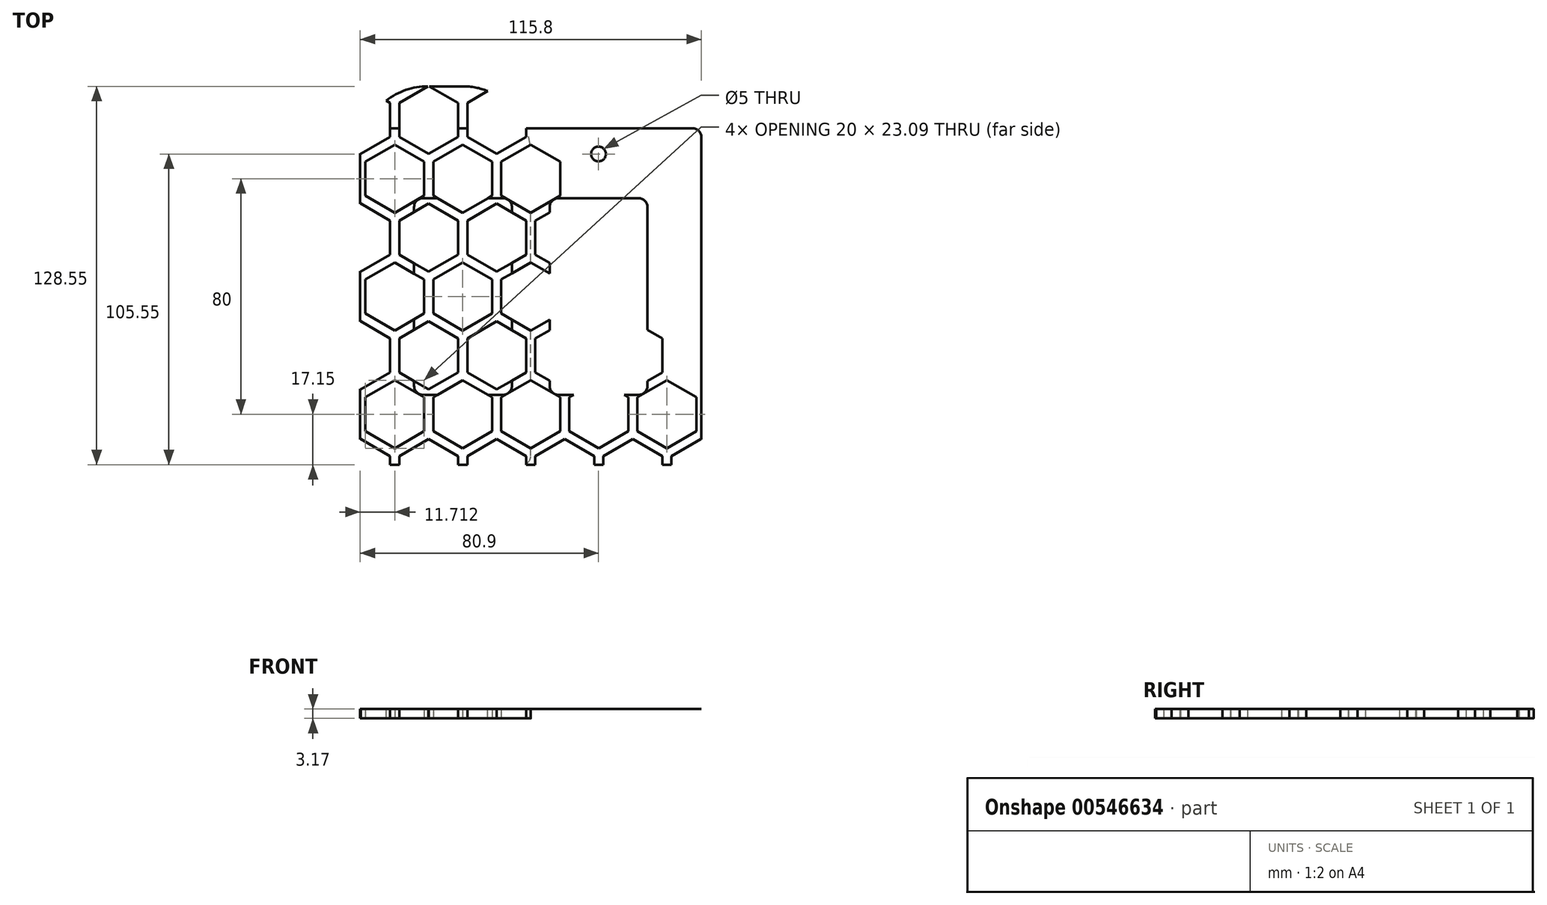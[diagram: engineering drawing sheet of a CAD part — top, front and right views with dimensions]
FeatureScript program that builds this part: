
annotation { "Feature Type Name" : "Feature", "Feature Type Description" : "" }
export const myFeature = defineFeature(function(context is Context, id is Id, definition is map)
    precondition{}
    {
        {
            var Q0;
            Q0=qCreatedBy(makeId("Top.planeOp"),FACE);
            var sketch = newSketch(context, id + "F0", { "sketchPlane" : qUnion([Q0])});
            skLineSegment(sketch, "E0", {"start": v(0, 57.15) * mm, "end": v(0, -57.15) * mm});
            skLineSegment(sketch, "E1.bottom", {"start": v(-6.4, -33.4) * mm, "end": v(-39.6, -33.4) * mm});
            skLineSegment(sketch, "E1.top", {"start": v(-6.4, 33.4) * mm, "end": v(-39.6, 33.4) * mm});
            skLineSegment(sketch, "E1.left", {"start": v(-6.4, -33.4) * mm, "end": v(-6.4, 33.4) * mm});
            skLineSegment(sketch, "E1.right", {"start": v(-39.6, -33.4) * mm, "end": v(-39.6, 33.4) * mm});
            skPoint(sketch, "E1.middle", {"position": v(-23, 0) * mm});
            skLineSegment(sketch, "E2.bottom", {"start": v(0, 57.15) * mm, "end": v(-57.9, 57.15) * mm});
            skLineSegment(sketch, "E2.top", {"start": v(0, -57.15) * mm, "end": v(-57.9, -57.15) * mm});
            skLineSegment(sketch, "E2.right", {"start": v(-57.9, 57.15) * mm, "end": v(-57.9, -57.15) * mm});
            skPoint(sketch, "E2.middle", {"position": v(-28.95, 0) * mm});
            skCircle(sketch, "E3", {"center": v(-23, 48.4) * mm, "radius": 2.5 * mm});
            skLineSegment(sketch, "E4", {"start": v(-23, 48.4) * mm, "end": v(-23, -48.4) * mm, "construction": true});
            skCircle(sketch, "E5", {"center": v(-23, -48.4) * mm, "radius": 2.5 * mm});
            skSolve(sketch);
        }
        {
            var Q0;
            Q0 = qSketchRegion(id + "F0", true);
            var Q1;
            Q1 = qConstructionFilter(qBodyType(qCreatedBy(id + "F0" ,EDGE), BodyType.WIRE), ConstructionObject.NO);
            extrude(context, id + "F1", {"entities" : qUnion([Q0]), "surfaceEntities" : qUnion([Q1]), "depth" : 1 / 203.2 * mm, "offsetDistance" : 25 * mm});
        }
        {
            var Q0;
            Q0=qCreatedBy(makeId("Top.planeOp"),FACE);
            var sketch = newSketch(context, id + "F2", { "sketchPlane" : qUnion([Q0])});
            skLineSegment(sketch, "E6.0.1", {"start": v(-57.9, 48.4) * mm, "end": v(-57.9, -57.15) * mm});
            skLineSegment(sketch, "E6.0.2", {"start": v(-57.9, -57.15) * mm, "end": v(0, -57.15) * mm});
            skLineSegment(sketch, "E6.0.3", {"start": v(0, -57.15) * mm, "end": v(0, 48.4) * mm});
            skCircle(sketch, "E7.0", {"center": v(-23, 48.4) * mm, "radius": 2.5 * mm});
            skLineSegment(sketch, "E7.1", {"start": v(-6.4, 33.4) * mm, "end": v(-39.6, 33.4) * mm, "construction": true});
            skLineSegment(sketch, "E7.2", {"start": v(-39.6, -33.4) * mm, "end": v(-39.6, 33.4) * mm, "construction": true});
            skLineSegment(sketch, "E7.3", {"start": v(-6.4, -33.4) * mm, "end": v(-6.4, 33.4) * mm, "construction": true});
            skLineSegment(sketch, "E7.4", {"start": v(-6.4, -33.4) * mm, "end": v(-39.6, -33.4) * mm, "construction": true});
            skCircle(sketch, "E8.0", {"center": v(-23, -48.4) * mm, "radius": 2.5 * mm});
            skLineSegment(sketch, "E9", {"start": v(0, 48.4) * mm, "end": v(0, 48.4) * mm});
            skArc(sketch, "E10", {"start": v(0, 48.4) * mm, "mid": v(-6.74, 64.66) * mm, "end": v(-23, 71.4) * mm});
            skArc(sketch, "E11", {"start": v(-57.9, 48.4) * mm, "mid": v(-51.16, 64.66) * mm, "end": v(-34.9, 71.4) * mm});
            skLineSegment(sketch, "E12", {"start": v(-34.9, 71.4) * mm, "end": v(-23, 71.4) * mm});
            skSolve(sketch);
        }
        {
            var Q0;
            Q0 = qSketchRegion(id + "F2", true);
            extrude(context, id + "F3", {"entities" : qUnion([Q0]), "oppositeDirection" : true, "depth" : 25.4 * mm / 8, "offsetDistance" : 25 * mm});
        }
        {
            var Q0;
            Q0=makeQuery(id+"F1.opExtrude","SWEPT_EDGE",EDGE,{"disambiguationData":[OSD([sQuery(id+"F0.wireOp",EDGE,"E2.bottom"),sQuery(id+"F0.wireOp",EDGE,"E2.right")])]});
            var Q1;
            Q1=makeQuery(id+"F1.opExtrude","SWEPT_EDGE",EDGE,{"disambiguationData":[OSD([sQuery(id+"F0.wireOp",EDGE,"E2.top"),sQuery(id+"F0.wireOp",EDGE,"E2.right")])]});
            var Q2;
            Q2=makeQuery(id+"F1.opExtrude","SWEPT_EDGE",EDGE,{"disambiguationData":[OSD([sQuery(id+"F0.wireOp",EDGE,"E1.top"),sQuery(id+"F0.wireOp",EDGE,"E1.right")])]});
            var Q3;
            Q3=makeQuery(id+"F1.opExtrude","SWEPT_EDGE",EDGE,{"disambiguationData":[OSD([sQuery(id+"F0.wireOp",EDGE,"E1.bottom"),sQuery(id+"F0.wireOp",EDGE,"E1.right")])]});
            var Q4;
            Q4=makeQuery(id+"F1.opExtrude","SWEPT_EDGE",EDGE,{"disambiguationData":[OSD([sQuery(id+"F0.wireOp",EDGE,"E1.bottom"),sQuery(id+"F0.wireOp",EDGE,"E1.left")])]});
            var Q5;
            Q5=makeQuery(id+"F1.opExtrude","SWEPT_EDGE",EDGE,{"disambiguationData":[OSD([sQuery(id+"F0.wireOp",EDGE,"E1.top"),sQuery(id+"F0.wireOp",EDGE,"E1.left")])]});
            var Q6;
            Q6=makeQuery(id+"F3.opExtrude","SWEPT_EDGE",EDGE,{"disambiguationData":[OSD([sQuery(id+"F2.wireOp",EDGE,"E6.0.0"),sQuery(id+"F2.wireOp",EDGE,"E6.0.3")])]});
            var Q7;
            Q7=makeQuery(id+"F3.opExtrude","SWEPT_EDGE",EDGE,{"disambiguationData":[OSD([sQuery(id+"F2.wireOp",EDGE,"E6.0.0"),sQuery(id+"F2.wireOp",EDGE,"E6.0.1")])]});
            var Q8;
            Q8=makeQuery(id+"F3.opExtrude","SWEPT_EDGE",EDGE,{"disambiguationData":[OSD([sQuery(id+"F2.wireOp",EDGE,"E6.0.2"),sQuery(id+"F2.wireOp",EDGE,"E6.0.3")])]});
            var Q9;
            Q9=makeQuery(id+"F3.opExtrude","SWEPT_EDGE",EDGE,{"disambiguationData":[OSD([sQuery(id+"F2.wireOp",EDGE,"E6.0.1"),sQuery(id+"F2.wireOp",EDGE,"E6.0.2")])]});
            fillet(context, id + "F4", {"entities" : qUnion([Q0, Q1, Q2, Q3, Q4, Q5, Q6, Q7, Q8, Q9]), "radius" : 3 * mm, "tangentPropagation" : true, "allowEdgeOverflow" : false});
        }
        {
            var Q0;
            Q0=makeQuery(id+"F1.opExtrude","SWEPT_BODY",BODY,{"disambiguationData":[OSD([sQuery(id+"F0.wireOp",EDGE,"E0"),sQuery(id+"F0.wireOp",EDGE,"E1.bottom"),sQuery(id+"F0.wireOp",EDGE,"E1.top"),sQuery(id+"F0.wireOp",EDGE,"E1.left"),sQuery(id+"F0.wireOp",EDGE,"E1.right"),sQuery(id+"F0.wireOp",EDGE,"E2.bottom"),sQuery(id+"F0.wireOp",EDGE,"E2.top"),sQuery(id+"F0.wireOp",EDGE,"E2.right"),sQuery(id+"F0.wireOp",EDGE,"E3"),sQuery(id+"F0.wireOp",EDGE,"E5")])]});
            var Q1;
            Q1=makeQuery(id+"F1.opExtrude","SWEPT_FACE",FACE,{"disambiguationData":[OSD([sQuery(id+"F0.wireOp",EDGE,"E0")])]});
            mirror(context, id + "F5", {"operationType" : NewBodyOperationType.ADD, "entities" : qUnion([Q0]), "mirrorPlane" : qUnion([Q1])});
        }
        {
            var Q0;
            Q0=makeQuery(id+"F3.opExtrude","CAP_FACE",FACE,{"disambiguationData":[OSD([sQuery(id+"F2.wireOp",EDGE,"E6.0.1"),sQuery(id+"F2.wireOp",EDGE,"E6.0.2"),sQuery(id+"F2.wireOp",EDGE,"E6.0.3"),sQuery(id+"F2.wireOp",EDGE,"E7.0"),sQuery(id+"F2.wireOp",EDGE,"E8.0"),sQuery(id+"F2.wireOp",EDGE,"E10"),sQuery(id+"F2.wireOp",EDGE,"E11"),sQuery(id+"F2.wireOp",EDGE,"E12")])],"isStart":false});
            var sketch = newSketch(context, id + "F6", { "sketchPlane" : qUnion([Q0])});
            skCircle(sketch, "E13.cCircle", {"center": v(57.74, 60) * mm, "radius": 11.55 * mm, "construction": true});
            skLineSegment(sketch, "E13.0", {"start": v(47.74, 65.77) * mm, "end": v(57.74, 71.55) * mm});
            skLineSegment(sketch, "E13.1", {"start": v(57.74, 71.55) * mm, "end": v(67.74, 65.77) * mm});
            skLineSegment(sketch, "E13.2", {"start": v(67.74, 65.77) * mm, "end": v(67.74, 54.23) * mm});
            skLineSegment(sketch, "E13.3", {"start": v(67.74, 54.23) * mm, "end": v(57.74, 48.45) * mm});
            skLineSegment(sketch, "E13.4", {"start": v(57.74, 48.45) * mm, "end": v(47.74, 54.23) * mm});
            skLineSegment(sketch, "E13.5", {"start": v(47.74, 54.23) * mm, "end": v(47.74, 65.77) * mm});
            skLineSegment(sketch, "E14.0.1.0", {"start": v(36.19, 34.23) * mm, "end": v(36.19, 45.77) * mm});
            skLineSegment(sketch, "E14.0.1.1", {"start": v(46.19, 28.45) * mm, "end": v(36.19, 34.23) * mm});
            skLineSegment(sketch, "E14.0.1.2", {"start": v(56.19, 34.23) * mm, "end": v(46.19, 28.45) * mm});
            skLineSegment(sketch, "E14.0.1.3", {"start": v(56.19, 45.77) * mm, "end": v(56.19, 34.23) * mm});
            skLineSegment(sketch, "E14.0.1.4", {"start": v(46.19, 51.55) * mm, "end": v(56.19, 45.77) * mm});
            skCircle(sketch, "E14.0.1.5", {"center": v(46.19, 40) * mm, "radius": 11.55 * mm, "construction": true});
            skLineSegment(sketch, "E14.0.1.6", {"start": v(36.19, 45.77) * mm, "end": v(46.19, 51.55) * mm});
            skLineSegment(sketch, "E14.0.2.0", {"start": v(24.64, 14.23) * mm, "end": v(24.64, 25.77) * mm});
            skLineSegment(sketch, "E14.0.2.1", {"start": v(34.64, 8.45) * mm, "end": v(24.64, 14.23) * mm});
            skLineSegment(sketch, "E14.0.2.2", {"start": v(44.64, 14.23) * mm, "end": v(34.64, 8.45) * mm});
            skLineSegment(sketch, "E14.0.2.3", {"start": v(44.64, 25.77) * mm, "end": v(44.64, 14.23) * mm});
            skLineSegment(sketch, "E14.0.2.4", {"start": v(34.64, 31.55) * mm, "end": v(44.64, 25.77) * mm});
            skCircle(sketch, "E14.0.2.5", {"center": v(34.64, 20) * mm, "radius": 11.55 * mm, "construction": true});
            skLineSegment(sketch, "E14.0.2.6", {"start": v(24.64, 25.77) * mm, "end": v(34.64, 31.55) * mm});
            skLineSegment(sketch, "E14.0.3.0", {"start": v(13.1, -5.77) * mm, "end": v(13.1, 5.77) * mm});
            skLineSegment(sketch, "E14.0.3.1", {"start": v(23.1, -11.55) * mm, "end": v(13.1, -5.77) * mm});
            skLineSegment(sketch, "E14.0.3.2", {"start": v(33.1, -5.77) * mm, "end": v(23.1, -11.55) * mm});
            skLineSegment(sketch, "E14.0.3.3", {"start": v(33.1, 5.77) * mm, "end": v(33.1, -5.77) * mm});
            skLineSegment(sketch, "E14.0.3.4", {"start": v(23.1, 11.55) * mm, "end": v(33.1, 5.77) * mm});
            skCircle(sketch, "E14.0.3.5", {"center": v(23.1, 0) * mm, "radius": 11.55 * mm, "construction": true});
            skLineSegment(sketch, "E14.0.3.6", {"start": v(13.1, 5.77) * mm, "end": v(23.1, 11.55) * mm});
            skLineSegment(sketch, "E14.0.4.0", {"start": v(1.55, -25.77) * mm, "end": v(1.55, -14.23) * mm});
            skLineSegment(sketch, "E14.0.4.1", {"start": v(11.55, -31.55) * mm, "end": v(1.55, -25.77) * mm});
            skLineSegment(sketch, "E14.0.4.2", {"start": v(21.55, -25.77) * mm, "end": v(11.55, -31.55) * mm});
            skLineSegment(sketch, "E14.0.4.3", {"start": v(21.55, -14.23) * mm, "end": v(21.55, -25.77) * mm});
            skLineSegment(sketch, "E14.0.4.4", {"start": v(11.55, -8.45) * mm, "end": v(21.55, -14.23) * mm});
            skCircle(sketch, "E14.0.4.5", {"center": v(11.55, -20) * mm, "radius": 11.55 * mm, "construction": true});
            skLineSegment(sketch, "E14.0.4.6", {"start": v(1.55, -14.23) * mm, "end": v(11.55, -8.45) * mm});
            skLineSegment(sketch, "E14.1.0.0", {"start": v(24.64, 54.23) * mm, "end": v(24.64, 65.77) * mm});
            skLineSegment(sketch, "E14.1.0.1", {"start": v(34.64, 48.45) * mm, "end": v(24.64, 54.23) * mm});
            skLineSegment(sketch, "E14.1.0.2", {"start": v(44.64, 54.23) * mm, "end": v(34.64, 48.45) * mm});
            skLineSegment(sketch, "E14.1.0.3", {"start": v(44.64, 65.77) * mm, "end": v(44.64, 54.23) * mm});
            skLineSegment(sketch, "E14.1.0.4", {"start": v(34.64, 71.55) * mm, "end": v(44.64, 65.77) * mm});
            skCircle(sketch, "E14.1.0.5", {"center": v(34.64, 60) * mm, "radius": 11.55 * mm, "construction": true});
            skLineSegment(sketch, "E14.1.0.6", {"start": v(24.64, 65.77) * mm, "end": v(34.64, 71.55) * mm});
            skLineSegment(sketch, "E14.1.1.0", {"start": v(13.1, 34.23) * mm, "end": v(13.1, 45.77) * mm});
            skLineSegment(sketch, "E14.1.1.1", {"start": v(23.1, 28.45) * mm, "end": v(13.1, 34.23) * mm});
            skLineSegment(sketch, "E14.1.1.2", {"start": v(33.1, 34.23) * mm, "end": v(23.1, 28.45) * mm});
            skLineSegment(sketch, "E14.1.1.3", {"start": v(33.1, 45.77) * mm, "end": v(33.1, 34.23) * mm});
            skLineSegment(sketch, "E14.1.1.4", {"start": v(23.1, 51.55) * mm, "end": v(33.1, 45.77) * mm});
            skCircle(sketch, "E14.1.1.5", {"center": v(23.1, 40) * mm, "radius": 11.55 * mm, "construction": true});
            skLineSegment(sketch, "E14.1.1.6", {"start": v(13.1, 45.77) * mm, "end": v(23.1, 51.55) * mm});
            skLineSegment(sketch, "E14.1.2.0", {"start": v(1.55, 14.23) * mm, "end": v(1.55, 25.77) * mm});
            skLineSegment(sketch, "E14.1.2.1", {"start": v(11.55, 8.45) * mm, "end": v(1.55, 14.23) * mm});
            skLineSegment(sketch, "E14.1.2.2", {"start": v(21.55, 14.23) * mm, "end": v(11.55, 8.45) * mm});
            skLineSegment(sketch, "E14.1.2.3", {"start": v(21.55, 25.77) * mm, "end": v(21.55, 14.23) * mm});
            skLineSegment(sketch, "E14.1.2.4", {"start": v(11.55, 31.55) * mm, "end": v(21.55, 25.77) * mm});
            skCircle(sketch, "E14.1.2.5", {"center": v(11.55, 20) * mm, "radius": 11.55 * mm, "construction": true});
            skLineSegment(sketch, "E14.1.2.6", {"start": v(1.55, 25.77) * mm, "end": v(11.55, 31.55) * mm});
            skLineSegment(sketch, "E14.1.3.0", {"start": v(-10, -5.77) * mm, "end": v(-10, 5.77) * mm});
            skLineSegment(sketch, "E14.1.3.1", {"start": v(0, -11.55) * mm, "end": v(-10, -5.77) * mm});
            skLineSegment(sketch, "E14.1.3.2", {"start": v(10, -5.77) * mm, "end": v(0, -11.55) * mm});
            skLineSegment(sketch, "E14.1.3.3", {"start": v(10, 5.77) * mm, "end": v(10, -5.77) * mm});
            skLineSegment(sketch, "E14.1.3.4", {"start": v(0, 11.55) * mm, "end": v(10, 5.77) * mm});
            skCircle(sketch, "E14.1.3.5", {"center": v(0, 0) * mm, "radius": 11.55 * mm, "construction": true});
            skLineSegment(sketch, "E14.1.3.6", {"start": v(-10, 5.77) * mm, "end": v(0, 11.55) * mm});
            skLineSegment(sketch, "E14.1.4.0", {"start": v(-21.55, -25.77) * mm, "end": v(-21.55, -14.23) * mm});
            skLineSegment(sketch, "E14.1.4.1", {"start": v(-11.55, -31.55) * mm, "end": v(-21.55, -25.77) * mm});
            skLineSegment(sketch, "E14.1.4.2", {"start": v(-1.55, -25.77) * mm, "end": v(-11.55, -31.55) * mm});
            skLineSegment(sketch, "E14.1.4.3", {"start": v(-1.55, -14.23) * mm, "end": v(-1.55, -25.77) * mm});
            skLineSegment(sketch, "E14.1.4.4", {"start": v(-11.55, -8.45) * mm, "end": v(-1.55, -14.23) * mm});
            skCircle(sketch, "E14.1.4.5", {"center": v(-11.55, -20) * mm, "radius": 11.55 * mm, "construction": true});
            skLineSegment(sketch, "E14.1.4.6", {"start": v(-21.55, -14.23) * mm, "end": v(-11.55, -8.45) * mm});
            skLineSegment(sketch, "E14.2.0.0", {"start": v(1.55, 54.23) * mm, "end": v(1.55, 65.77) * mm});
            skLineSegment(sketch, "E14.2.0.1", {"start": v(11.55, 48.45) * mm, "end": v(1.55, 54.23) * mm});
            skLineSegment(sketch, "E14.2.0.2", {"start": v(21.55, 54.23) * mm, "end": v(11.55, 48.45) * mm});
            skLineSegment(sketch, "E14.2.0.3", {"start": v(21.55, 65.77) * mm, "end": v(21.55, 54.23) * mm});
            skLineSegment(sketch, "E14.2.0.4", {"start": v(11.55, 71.55) * mm, "end": v(21.55, 65.77) * mm});
            skCircle(sketch, "E14.2.0.5", {"center": v(11.55, 60) * mm, "radius": 11.55 * mm, "construction": true});
            skLineSegment(sketch, "E14.2.0.6", {"start": v(1.55, 65.77) * mm, "end": v(11.55, 71.55) * mm});
            skLineSegment(sketch, "E14.2.1.0", {"start": v(-10, 34.23) * mm, "end": v(-10, 45.77) * mm});
            skLineSegment(sketch, "E14.2.1.1", {"start": v(0, 28.45) * mm, "end": v(-10, 34.23) * mm});
            skLineSegment(sketch, "E14.2.1.2", {"start": v(10, 34.23) * mm, "end": v(0, 28.45) * mm});
            skLineSegment(sketch, "E14.2.1.3", {"start": v(10, 45.77) * mm, "end": v(10, 34.23) * mm});
            skLineSegment(sketch, "E14.2.1.4", {"start": v(0, 51.55) * mm, "end": v(10, 45.77) * mm});
            skCircle(sketch, "E14.2.1.5", {"center": v(0, 40) * mm, "radius": 11.55 * mm, "construction": true});
            skLineSegment(sketch, "E14.2.1.6", {"start": v(-10, 45.77) * mm, "end": v(0, 51.55) * mm});
            skLineSegment(sketch, "E14.2.2.0", {"start": v(-21.55, 14.23) * mm, "end": v(-21.55, 25.77) * mm});
            skLineSegment(sketch, "E14.2.2.1", {"start": v(-11.55, 8.45) * mm, "end": v(-21.55, 14.23) * mm});
            skLineSegment(sketch, "E14.2.2.2", {"start": v(-1.55, 14.23) * mm, "end": v(-11.55, 8.45) * mm});
            skLineSegment(sketch, "E14.2.2.3", {"start": v(-1.55, 25.77) * mm, "end": v(-1.55, 14.23) * mm});
            skLineSegment(sketch, "E14.2.2.4", {"start": v(-11.55, 31.55) * mm, "end": v(-1.55, 25.77) * mm});
            skCircle(sketch, "E14.2.2.5", {"center": v(-11.55, 20) * mm, "radius": 11.55 * mm, "construction": true});
            skLineSegment(sketch, "E14.2.2.6", {"start": v(-21.55, 25.77) * mm, "end": v(-11.55, 31.55) * mm});
            skLineSegment(sketch, "E14.2.3.0", {"start": v(-33.1, -5.77) * mm, "end": v(-33.1, 5.77) * mm});
            skLineSegment(sketch, "E14.2.3.1", {"start": v(-23.1, -11.55) * mm, "end": v(-33.1, -5.77) * mm});
            skLineSegment(sketch, "E14.2.3.2", {"start": v(-13.1, -5.77) * mm, "end": v(-23.1, -11.55) * mm});
            skLineSegment(sketch, "E14.2.3.3", {"start": v(-13.1, 5.77) * mm, "end": v(-13.1, -5.77) * mm});
            skLineSegment(sketch, "E14.2.3.4", {"start": v(-23.1, 11.55) * mm, "end": v(-13.1, 5.77) * mm});
            skCircle(sketch, "E14.2.3.5", {"center": v(-23.1, 0) * mm, "radius": 11.55 * mm, "construction": true});
            skLineSegment(sketch, "E14.2.3.6", {"start": v(-33.1, 5.77) * mm, "end": v(-23.1, 11.55) * mm});
            skLineSegment(sketch, "E14.2.4.0", {"start": v(-44.64, -25.77) * mm, "end": v(-44.64, -14.23) * mm});
            skLineSegment(sketch, "E14.2.4.1", {"start": v(-34.64, -31.55) * mm, "end": v(-44.64, -25.77) * mm});
            skLineSegment(sketch, "E14.2.4.2", {"start": v(-24.64, -25.77) * mm, "end": v(-34.64, -31.55) * mm});
            skLineSegment(sketch, "E14.2.4.3", {"start": v(-24.64, -14.23) * mm, "end": v(-24.64, -25.77) * mm});
            skLineSegment(sketch, "E14.2.4.4", {"start": v(-34.64, -8.45) * mm, "end": v(-24.64, -14.23) * mm});
            skCircle(sketch, "E14.2.4.5", {"center": v(-34.64, -20) * mm, "radius": 11.55 * mm, "construction": true});
            skLineSegment(sketch, "E14.2.4.6", {"start": v(-44.64, -14.23) * mm, "end": v(-34.64, -8.45) * mm});
            skLineSegment(sketch, "E14.direction1", {"start": v(47.74, 54.23) * mm, "end": v(24.64, 54.23) * mm, "construction": true});
            skLineSegment(sketch, "E14.direction2", {"start": v(47.74, 54.23) * mm, "end": v(36.19, 34.23) * mm, "construction": true});
            skLineSegment(sketch, "E15.0.0.5", {"start": v(-10, -45.77) * mm, "end": v(-10, -34.23) * mm});
            skLineSegment(sketch, "E15.3.0.5", {"start": v(0, -51.55) * mm, "end": v(-10, -45.77) * mm});
            skLineSegment(sketch, "E15.6.0.5", {"start": v(10, -45.77) * mm, "end": v(0, -51.55) * mm});
            skLineSegment(sketch, "E15.9.0.5", {"start": v(10, -34.23) * mm, "end": v(10, -45.77) * mm});
            skLineSegment(sketch, "E15.12.0.5", {"start": v(0, -28.45) * mm, "end": v(10, -34.23) * mm});
            skCircle(sketch, "E15.15.0.5", {"center": v(0, -40) * mm, "radius": 11.55 * mm, "construction": true});
            skLineSegment(sketch, "E15.17.0.5", {"start": v(-10, -34.23) * mm, "end": v(0, -28.45) * mm});
            skLineSegment(sketch, "E15.0.0.6", {"start": v(-21.55, -65.77) * mm, "end": v(-21.55, -54.23) * mm});
            skLineSegment(sketch, "E15.3.0.6", {"start": v(-11.55, -71.55) * mm, "end": v(-21.55, -65.77) * mm});
            skLineSegment(sketch, "E15.6.0.6", {"start": v(-1.55, -65.77) * mm, "end": v(-11.55, -71.55) * mm});
            skLineSegment(sketch, "E15.9.0.6", {"start": v(-1.55, -54.23) * mm, "end": v(-1.55, -65.77) * mm});
            skLineSegment(sketch, "E15.12.0.6", {"start": v(-11.55, -48.45) * mm, "end": v(-1.55, -54.23) * mm});
            skCircle(sketch, "E15.15.0.6", {"center": v(-11.55, -60) * mm, "radius": 11.55 * mm, "construction": true});
            skLineSegment(sketch, "E15.17.0.6", {"start": v(-21.55, -54.23) * mm, "end": v(-11.55, -48.45) * mm});
            skLineSegment(sketch, "E15.0.1.5", {"start": v(-33.1, -45.77) * mm, "end": v(-33.1, -34.23) * mm});
            skLineSegment(sketch, "E15.3.1.5", {"start": v(-23.1, -51.55) * mm, "end": v(-33.1, -45.77) * mm});
            skLineSegment(sketch, "E15.6.1.5", {"start": v(-13.1, -45.77) * mm, "end": v(-23.1, -51.55) * mm});
            skLineSegment(sketch, "E15.9.1.5", {"start": v(-13.1, -34.23) * mm, "end": v(-13.1, -45.77) * mm});
            skLineSegment(sketch, "E15.12.1.5", {"start": v(-23.1, -28.45) * mm, "end": v(-13.1, -34.23) * mm});
            skCircle(sketch, "E15.15.1.5", {"center": v(-23.1, -40) * mm, "radius": 11.55 * mm, "construction": true});
            skLineSegment(sketch, "E15.17.1.5", {"start": v(-33.1, -34.23) * mm, "end": v(-23.1, -28.45) * mm});
            skLineSegment(sketch, "E15.0.1.6", {"start": v(-44.64, -65.77) * mm, "end": v(-44.64, -54.23) * mm});
            skLineSegment(sketch, "E15.3.1.6", {"start": v(-34.64, -71.55) * mm, "end": v(-44.64, -65.77) * mm});
            skLineSegment(sketch, "E15.6.1.6", {"start": v(-24.64, -65.77) * mm, "end": v(-34.64, -71.55) * mm});
            skLineSegment(sketch, "E15.9.1.6", {"start": v(-24.64, -54.23) * mm, "end": v(-24.64, -65.77) * mm});
            skLineSegment(sketch, "E15.12.1.6", {"start": v(-34.64, -48.45) * mm, "end": v(-24.64, -54.23) * mm});
            skCircle(sketch, "E15.15.1.6", {"center": v(-34.64, -60) * mm, "radius": 11.55 * mm, "construction": true});
            skLineSegment(sketch, "E15.17.1.6", {"start": v(-44.64, -54.23) * mm, "end": v(-34.64, -48.45) * mm});
            skLineSegment(sketch, "E15.0.2.5", {"start": v(-56.19, -45.77) * mm, "end": v(-56.19, -34.23) * mm});
            skLineSegment(sketch, "E15.3.2.5", {"start": v(-46.19, -51.55) * mm, "end": v(-56.19, -45.77) * mm});
            skLineSegment(sketch, "E15.6.2.5", {"start": v(-36.19, -45.77) * mm, "end": v(-46.19, -51.55) * mm});
            skLineSegment(sketch, "E15.9.2.5", {"start": v(-36.19, -34.23) * mm, "end": v(-36.19, -45.77) * mm});
            skLineSegment(sketch, "E15.12.2.5", {"start": v(-46.19, -28.45) * mm, "end": v(-36.19, -34.23) * mm});
            skCircle(sketch, "E15.15.2.5", {"center": v(-46.19, -40) * mm, "radius": 11.55 * mm, "construction": true});
            skLineSegment(sketch, "E15.17.2.5", {"start": v(-56.19, -34.23) * mm, "end": v(-46.19, -28.45) * mm});
            skLineSegment(sketch, "E15.0.2.6", {"start": v(-67.74, -65.77) * mm, "end": v(-67.74, -54.23) * mm});
            skLineSegment(sketch, "E15.3.2.6", {"start": v(-57.74, -71.55) * mm, "end": v(-67.74, -65.77) * mm});
            skLineSegment(sketch, "E15.6.2.6", {"start": v(-47.74, -65.77) * mm, "end": v(-57.74, -71.55) * mm});
            skLineSegment(sketch, "E15.9.2.6", {"start": v(-47.74, -54.23) * mm, "end": v(-47.74, -65.77) * mm});
            skLineSegment(sketch, "E15.12.2.6", {"start": v(-57.74, -48.45) * mm, "end": v(-47.74, -54.23) * mm});
            skCircle(sketch, "E15.15.2.6", {"center": v(-57.74, -60) * mm, "radius": 11.55 * mm, "construction": true});
            skLineSegment(sketch, "E15.17.2.6", {"start": v(-67.74, -54.23) * mm, "end": v(-57.74, -48.45) * mm});
            skLineSegment(sketch, "E16.0.3.0", {"start": v(-21.55, 54.23) * mm, "end": v(-21.55, 65.77) * mm});
            skLineSegment(sketch, "E16.3.3.0", {"start": v(-11.55, 48.45) * mm, "end": v(-21.55, 54.23) * mm});
            skLineSegment(sketch, "E16.6.3.0", {"start": v(-1.55, 54.23) * mm, "end": v(-11.55, 48.45) * mm});
            skLineSegment(sketch, "E16.9.3.0", {"start": v(-1.55, 65.77) * mm, "end": v(-1.55, 54.23) * mm});
            skLineSegment(sketch, "E16.12.3.0", {"start": v(-11.55, 71.55) * mm, "end": v(-1.55, 65.77) * mm});
            skCircle(sketch, "E16.15.3.0", {"center": v(-11.55, 60) * mm, "radius": 11.55 * mm, "construction": true});
            skLineSegment(sketch, "E16.17.3.0", {"start": v(-21.55, 65.77) * mm, "end": v(-11.55, 71.55) * mm});
            skLineSegment(sketch, "E16.0.3.1", {"start": v(-33.1, 34.23) * mm, "end": v(-33.1, 45.77) * mm});
            skLineSegment(sketch, "E16.3.3.1", {"start": v(-23.1, 28.45) * mm, "end": v(-33.1, 34.23) * mm});
            skLineSegment(sketch, "E16.6.3.1", {"start": v(-13.1, 34.23) * mm, "end": v(-23.1, 28.45) * mm});
            skLineSegment(sketch, "E16.9.3.1", {"start": v(-13.1, 45.77) * mm, "end": v(-13.1, 34.23) * mm});
            skLineSegment(sketch, "E16.12.3.1", {"start": v(-23.1, 51.55) * mm, "end": v(-13.1, 45.77) * mm});
            skCircle(sketch, "E16.15.3.1", {"center": v(-23.1, 40) * mm, "radius": 11.55 * mm, "construction": true});
            skLineSegment(sketch, "E16.17.3.1", {"start": v(-33.1, 45.77) * mm, "end": v(-23.1, 51.55) * mm});
            skLineSegment(sketch, "E16.0.3.2", {"start": v(-44.64, 14.23) * mm, "end": v(-44.64, 25.77) * mm});
            skLineSegment(sketch, "E16.3.3.2", {"start": v(-34.64, 8.45) * mm, "end": v(-44.64, 14.23) * mm});
            skLineSegment(sketch, "E16.6.3.2", {"start": v(-24.64, 14.23) * mm, "end": v(-34.64, 8.45) * mm});
            skLineSegment(sketch, "E16.9.3.2", {"start": v(-24.64, 25.77) * mm, "end": v(-24.64, 14.23) * mm});
            skLineSegment(sketch, "E16.12.3.2", {"start": v(-34.64, 31.55) * mm, "end": v(-24.64, 25.77) * mm});
            skCircle(sketch, "E16.15.3.2", {"center": v(-34.64, 20) * mm, "radius": 11.55 * mm, "construction": true});
            skLineSegment(sketch, "E16.17.3.2", {"start": v(-44.64, 25.77) * mm, "end": v(-34.64, 31.55) * mm});
            skLineSegment(sketch, "E16.0.3.3", {"start": v(-56.19, -5.77) * mm, "end": v(-56.19, 5.77) * mm});
            skLineSegment(sketch, "E16.3.3.3", {"start": v(-46.19, -11.55) * mm, "end": v(-56.19, -5.77) * mm});
            skLineSegment(sketch, "E16.6.3.3", {"start": v(-36.19, -5.77) * mm, "end": v(-46.19, -11.55) * mm});
            skLineSegment(sketch, "E16.9.3.3", {"start": v(-36.19, 5.77) * mm, "end": v(-36.19, -5.77) * mm});
            skLineSegment(sketch, "E16.12.3.3", {"start": v(-46.19, 11.55) * mm, "end": v(-36.19, 5.77) * mm});
            skCircle(sketch, "E16.15.3.3", {"center": v(-46.19, 0) * mm, "radius": 11.55 * mm, "construction": true});
            skLineSegment(sketch, "E16.17.3.3", {"start": v(-56.19, 5.77) * mm, "end": v(-46.19, 11.55) * mm});
            skLineSegment(sketch, "E16.0.3.4", {"start": v(-67.74, -25.77) * mm, "end": v(-67.74, -14.23) * mm});
            skLineSegment(sketch, "E16.3.3.4", {"start": v(-57.74, -31.55) * mm, "end": v(-67.74, -25.77) * mm});
            skLineSegment(sketch, "E16.6.3.4", {"start": v(-47.74, -25.77) * mm, "end": v(-57.74, -31.55) * mm});
            skLineSegment(sketch, "E16.9.3.4", {"start": v(-47.74, -14.23) * mm, "end": v(-47.74, -25.77) * mm});
            skLineSegment(sketch, "E16.12.3.4", {"start": v(-57.74, -8.45) * mm, "end": v(-47.74, -14.23) * mm});
            skCircle(sketch, "E16.15.3.4", {"center": v(-57.74, -20) * mm, "radius": 11.55 * mm, "construction": true});
            skLineSegment(sketch, "E16.17.3.4", {"start": v(-67.74, -14.23) * mm, "end": v(-57.74, -8.45) * mm});
            skLineSegment(sketch, "E16.0.3.5", {"start": v(-79.28, -45.77) * mm, "end": v(-79.28, -34.23) * mm});
            skLineSegment(sketch, "E16.3.3.5", {"start": v(-69.28, -51.55) * mm, "end": v(-79.28, -45.77) * mm});
            skLineSegment(sketch, "E16.6.3.5", {"start": v(-59.28, -45.77) * mm, "end": v(-69.28, -51.55) * mm});
            skLineSegment(sketch, "E16.9.3.5", {"start": v(-59.28, -34.23) * mm, "end": v(-59.28, -45.77) * mm});
            skLineSegment(sketch, "E16.12.3.5", {"start": v(-69.28, -28.45) * mm, "end": v(-59.28, -34.23) * mm});
            skCircle(sketch, "E16.15.3.5", {"center": v(-69.28, -40) * mm, "radius": 11.55 * mm, "construction": true});
            skLineSegment(sketch, "E16.17.3.5", {"start": v(-79.28, -34.23) * mm, "end": v(-69.28, -28.45) * mm});
            skLineSegment(sketch, "E16.0.3.6", {"start": v(-90.83, -65.77) * mm, "end": v(-90.83, -54.23) * mm});
            skLineSegment(sketch, "E16.3.3.6", {"start": v(-80.83, -71.55) * mm, "end": v(-90.83, -65.77) * mm});
            skLineSegment(sketch, "E16.6.3.6", {"start": v(-70.83, -65.77) * mm, "end": v(-80.83, -71.55) * mm});
            skLineSegment(sketch, "E16.9.3.6", {"start": v(-70.83, -54.23) * mm, "end": v(-70.83, -65.77) * mm});
            skLineSegment(sketch, "E16.12.3.6", {"start": v(-80.83, -48.45) * mm, "end": v(-70.83, -54.23) * mm});
            skCircle(sketch, "E16.15.3.6", {"center": v(-80.83, -60) * mm, "radius": 11.55 * mm, "construction": true});
            skLineSegment(sketch, "E16.17.3.6", {"start": v(-90.83, -54.23) * mm, "end": v(-80.83, -48.45) * mm});
            skLineSegment(sketch, "E16.0.4.0", {"start": v(-44.64, 54.23) * mm, "end": v(-44.64, 65.77) * mm});
            skLineSegment(sketch, "E16.3.4.0", {"start": v(-34.64, 48.45) * mm, "end": v(-44.64, 54.23) * mm});
            skLineSegment(sketch, "E16.6.4.0", {"start": v(-24.64, 54.23) * mm, "end": v(-34.64, 48.45) * mm});
            skLineSegment(sketch, "E16.9.4.0", {"start": v(-24.64, 65.77) * mm, "end": v(-24.64, 54.23) * mm});
            skLineSegment(sketch, "E16.12.4.0", {"start": v(-34.64, 71.55) * mm, "end": v(-24.64, 65.77) * mm});
            skCircle(sketch, "E16.15.4.0", {"center": v(-34.64, 60) * mm, "radius": 11.55 * mm, "construction": true});
            skLineSegment(sketch, "E16.17.4.0", {"start": v(-44.64, 65.77) * mm, "end": v(-34.64, 71.55) * mm});
            skLineSegment(sketch, "E16.0.4.1", {"start": v(-56.19, 34.23) * mm, "end": v(-56.19, 45.77) * mm});
            skLineSegment(sketch, "E16.3.4.1", {"start": v(-46.19, 28.45) * mm, "end": v(-56.19, 34.23) * mm});
            skLineSegment(sketch, "E16.6.4.1", {"start": v(-36.19, 34.23) * mm, "end": v(-46.19, 28.45) * mm});
            skLineSegment(sketch, "E16.9.4.1", {"start": v(-36.19, 45.77) * mm, "end": v(-36.19, 34.23) * mm});
            skLineSegment(sketch, "E16.12.4.1", {"start": v(-46.19, 51.55) * mm, "end": v(-36.19, 45.77) * mm});
            skCircle(sketch, "E16.15.4.1", {"center": v(-46.19, 40) * mm, "radius": 11.55 * mm, "construction": true});
            skLineSegment(sketch, "E16.17.4.1", {"start": v(-56.19, 45.77) * mm, "end": v(-46.19, 51.55) * mm});
            skLineSegment(sketch, "E16.0.4.2", {"start": v(-67.74, 14.23) * mm, "end": v(-67.74, 25.77) * mm});
            skLineSegment(sketch, "E16.3.4.2", {"start": v(-57.74, 8.45) * mm, "end": v(-67.74, 14.23) * mm});
            skLineSegment(sketch, "E16.6.4.2", {"start": v(-47.74, 14.23) * mm, "end": v(-57.74, 8.45) * mm});
            skLineSegment(sketch, "E16.9.4.2", {"start": v(-47.74, 25.77) * mm, "end": v(-47.74, 14.23) * mm});
            skLineSegment(sketch, "E16.12.4.2", {"start": v(-57.74, 31.55) * mm, "end": v(-47.74, 25.77) * mm});
            skCircle(sketch, "E16.15.4.2", {"center": v(-57.74, 20) * mm, "radius": 11.55 * mm, "construction": true});
            skLineSegment(sketch, "E16.17.4.2", {"start": v(-67.74, 25.77) * mm, "end": v(-57.74, 31.55) * mm});
            skLineSegment(sketch, "E16.0.4.3", {"start": v(-79.28, -5.77) * mm, "end": v(-79.28, 5.77) * mm});
            skLineSegment(sketch, "E16.3.4.3", {"start": v(-69.28, -11.55) * mm, "end": v(-79.28, -5.77) * mm});
            skLineSegment(sketch, "E16.6.4.3", {"start": v(-59.28, -5.77) * mm, "end": v(-69.28, -11.55) * mm});
            skLineSegment(sketch, "E16.9.4.3", {"start": v(-59.28, 5.77) * mm, "end": v(-59.28, -5.77) * mm});
            skLineSegment(sketch, "E16.12.4.3", {"start": v(-69.28, 11.55) * mm, "end": v(-59.28, 5.77) * mm});
            skCircle(sketch, "E16.15.4.3", {"center": v(-69.28, 0) * mm, "radius": 11.55 * mm, "construction": true});
            skLineSegment(sketch, "E16.17.4.3", {"start": v(-79.28, 5.77) * mm, "end": v(-69.28, 11.55) * mm});
            skLineSegment(sketch, "E16.0.4.4", {"start": v(-90.83, -25.77) * mm, "end": v(-90.83, -14.23) * mm});
            skLineSegment(sketch, "E16.3.4.4", {"start": v(-80.83, -31.55) * mm, "end": v(-90.83, -25.77) * mm});
            skLineSegment(sketch, "E16.6.4.4", {"start": v(-70.83, -25.77) * mm, "end": v(-80.83, -31.55) * mm});
            skLineSegment(sketch, "E16.9.4.4", {"start": v(-70.83, -14.23) * mm, "end": v(-70.83, -25.77) * mm});
            skLineSegment(sketch, "E16.12.4.4", {"start": v(-80.83, -8.45) * mm, "end": v(-70.83, -14.23) * mm});
            skCircle(sketch, "E16.15.4.4", {"center": v(-80.83, -20) * mm, "radius": 11.55 * mm, "construction": true});
            skLineSegment(sketch, "E16.17.4.4", {"start": v(-90.83, -14.23) * mm, "end": v(-80.83, -8.45) * mm});
            skLineSegment(sketch, "E16.0.4.5", {"start": v(-102.38, -45.77) * mm, "end": v(-102.38, -34.23) * mm});
            skLineSegment(sketch, "E16.3.4.5", {"start": v(-92.38, -51.55) * mm, "end": v(-102.38, -45.77) * mm});
            skLineSegment(sketch, "E16.6.4.5", {"start": v(-82.38, -45.77) * mm, "end": v(-92.38, -51.55) * mm});
            skLineSegment(sketch, "E16.9.4.5", {"start": v(-82.38, -34.23) * mm, "end": v(-82.38, -45.77) * mm});
            skLineSegment(sketch, "E16.12.4.5", {"start": v(-92.38, -28.45) * mm, "end": v(-82.38, -34.23) * mm});
            skCircle(sketch, "E16.15.4.5", {"center": v(-92.38, -40) * mm, "radius": 11.55 * mm, "construction": true});
            skLineSegment(sketch, "E16.17.4.5", {"start": v(-102.38, -34.23) * mm, "end": v(-92.38, -28.45) * mm});
            skLineSegment(sketch, "E16.0.4.6", {"start": v(-113.92, -65.77) * mm, "end": v(-113.92, -54.23) * mm});
            skLineSegment(sketch, "E16.3.4.6", {"start": v(-103.92, -71.55) * mm, "end": v(-113.92, -65.77) * mm});
            skLineSegment(sketch, "E16.6.4.6", {"start": v(-93.92, -65.77) * mm, "end": v(-103.92, -71.55) * mm});
            skLineSegment(sketch, "E16.9.4.6", {"start": v(-93.92, -54.23) * mm, "end": v(-93.92, -65.77) * mm});
            skLineSegment(sketch, "E16.12.4.6", {"start": v(-103.92, -48.45) * mm, "end": v(-93.92, -54.23) * mm});
            skCircle(sketch, "E16.15.4.6", {"center": v(-103.92, -60) * mm, "radius": 11.55 * mm, "construction": true});
            skLineSegment(sketch, "E16.17.4.6", {"start": v(-113.92, -54.23) * mm, "end": v(-103.92, -48.45) * mm});
            skLineSegment(sketch, "E16.0.5.0", {"start": v(-67.74, 54.23) * mm, "end": v(-67.74, 65.77) * mm});
            skLineSegment(sketch, "E16.3.5.0", {"start": v(-57.74, 48.45) * mm, "end": v(-67.74, 54.23) * mm});
            skLineSegment(sketch, "E16.6.5.0", {"start": v(-47.74, 54.23) * mm, "end": v(-57.74, 48.45) * mm});
            skLineSegment(sketch, "E16.9.5.0", {"start": v(-47.74, 65.77) * mm, "end": v(-47.74, 54.23) * mm});
            skLineSegment(sketch, "E16.12.5.0", {"start": v(-57.74, 71.55) * mm, "end": v(-47.74, 65.77) * mm});
            skCircle(sketch, "E16.15.5.0", {"center": v(-57.74, 60) * mm, "radius": 11.55 * mm, "construction": true});
            skLineSegment(sketch, "E16.17.5.0", {"start": v(-67.74, 65.77) * mm, "end": v(-57.74, 71.55) * mm});
            skLineSegment(sketch, "E16.0.5.1", {"start": v(-79.28, 34.23) * mm, "end": v(-79.28, 45.77) * mm});
            skLineSegment(sketch, "E16.3.5.1", {"start": v(-69.28, 28.45) * mm, "end": v(-79.28, 34.23) * mm});
            skLineSegment(sketch, "E16.6.5.1", {"start": v(-59.28, 34.23) * mm, "end": v(-69.28, 28.45) * mm});
            skLineSegment(sketch, "E16.9.5.1", {"start": v(-59.28, 45.77) * mm, "end": v(-59.28, 34.23) * mm});
            skLineSegment(sketch, "E16.12.5.1", {"start": v(-69.28, 51.55) * mm, "end": v(-59.28, 45.77) * mm});
            skCircle(sketch, "E16.15.5.1", {"center": v(-69.28, 40) * mm, "radius": 11.55 * mm, "construction": true});
            skLineSegment(sketch, "E16.17.5.1", {"start": v(-79.28, 45.77) * mm, "end": v(-69.28, 51.55) * mm});
            skLineSegment(sketch, "E16.0.5.2", {"start": v(-90.83, 14.23) * mm, "end": v(-90.83, 25.77) * mm});
            skLineSegment(sketch, "E16.3.5.2", {"start": v(-80.83, 8.45) * mm, "end": v(-90.83, 14.23) * mm});
            skLineSegment(sketch, "E16.6.5.2", {"start": v(-70.83, 14.23) * mm, "end": v(-80.83, 8.45) * mm});
            skLineSegment(sketch, "E16.9.5.2", {"start": v(-70.83, 25.77) * mm, "end": v(-70.83, 14.23) * mm});
            skLineSegment(sketch, "E16.12.5.2", {"start": v(-80.83, 31.55) * mm, "end": v(-70.83, 25.77) * mm});
            skCircle(sketch, "E16.15.5.2", {"center": v(-80.83, 20) * mm, "radius": 11.55 * mm, "construction": true});
            skLineSegment(sketch, "E16.17.5.2", {"start": v(-90.83, 25.77) * mm, "end": v(-80.83, 31.55) * mm});
            skLineSegment(sketch, "E16.0.5.3", {"start": v(-102.38, -5.77) * mm, "end": v(-102.38, 5.77) * mm});
            skLineSegment(sketch, "E16.3.5.3", {"start": v(-92.38, -11.55) * mm, "end": v(-102.38, -5.77) * mm});
            skLineSegment(sketch, "E16.6.5.3", {"start": v(-82.38, -5.77) * mm, "end": v(-92.38, -11.55) * mm});
            skLineSegment(sketch, "E16.9.5.3", {"start": v(-82.38, 5.77) * mm, "end": v(-82.38, -5.77) * mm});
            skLineSegment(sketch, "E16.12.5.3", {"start": v(-92.38, 11.55) * mm, "end": v(-82.38, 5.77) * mm});
            skCircle(sketch, "E16.15.5.3", {"center": v(-92.38, 0) * mm, "radius": 11.55 * mm, "construction": true});
            skLineSegment(sketch, "E16.17.5.3", {"start": v(-102.38, 5.77) * mm, "end": v(-92.38, 11.55) * mm});
            skLineSegment(sketch, "E16.0.5.4", {"start": v(-113.92, -25.77) * mm, "end": v(-113.92, -14.23) * mm});
            skLineSegment(sketch, "E16.3.5.4", {"start": v(-103.92, -31.55) * mm, "end": v(-113.92, -25.77) * mm});
            skLineSegment(sketch, "E16.6.5.4", {"start": v(-93.92, -25.77) * mm, "end": v(-103.92, -31.55) * mm});
            skLineSegment(sketch, "E16.9.5.4", {"start": v(-93.92, -14.23) * mm, "end": v(-93.92, -25.77) * mm});
            skLineSegment(sketch, "E16.12.5.4", {"start": v(-103.92, -8.45) * mm, "end": v(-93.92, -14.23) * mm});
            skCircle(sketch, "E16.15.5.4", {"center": v(-103.92, -20) * mm, "radius": 11.55 * mm, "construction": true});
            skLineSegment(sketch, "E16.17.5.4", {"start": v(-113.92, -14.23) * mm, "end": v(-103.92, -8.45) * mm});
            skLineSegment(sketch, "E16.0.5.5", {"start": v(-125.47, -45.77) * mm, "end": v(-125.47, -34.23) * mm});
            skLineSegment(sketch, "E16.3.5.5", {"start": v(-115.47, -51.55) * mm, "end": v(-125.47, -45.77) * mm});
            skLineSegment(sketch, "E16.6.5.5", {"start": v(-105.47, -45.77) * mm, "end": v(-115.47, -51.55) * mm});
            skLineSegment(sketch, "E16.9.5.5", {"start": v(-105.47, -34.23) * mm, "end": v(-105.47, -45.77) * mm});
            skLineSegment(sketch, "E16.12.5.5", {"start": v(-115.47, -28.45) * mm, "end": v(-105.47, -34.23) * mm});
            skCircle(sketch, "E16.15.5.5", {"center": v(-115.47, -40) * mm, "radius": 11.55 * mm, "construction": true});
            skLineSegment(sketch, "E16.17.5.5", {"start": v(-125.47, -34.23) * mm, "end": v(-115.47, -28.45) * mm});
            skLineSegment(sketch, "E16.0.5.6", {"start": v(-137.02, -65.77) * mm, "end": v(-137.02, -54.23) * mm});
            skLineSegment(sketch, "E16.3.5.6", {"start": v(-127.02, -71.55) * mm, "end": v(-137.02, -65.77) * mm});
            skLineSegment(sketch, "E16.6.5.6", {"start": v(-117.02, -65.77) * mm, "end": v(-127.02, -71.55) * mm});
            skLineSegment(sketch, "E16.9.5.6", {"start": v(-117.02, -54.23) * mm, "end": v(-117.02, -65.77) * mm});
            skLineSegment(sketch, "E16.12.5.6", {"start": v(-127.02, -48.45) * mm, "end": v(-117.02, -54.23) * mm});
            skCircle(sketch, "E16.15.5.6", {"center": v(-127.02, -60) * mm, "radius": 11.55 * mm, "construction": true});
            skLineSegment(sketch, "E16.17.5.6", {"start": v(-137.02, -54.23) * mm, "end": v(-127.02, -48.45) * mm});
            skSolve(sketch);
        }
        {
            var Q0;
            Q0 = qSketchRegion(id + "F6", true);
            extrude(context, id + "F7", {"entities" : qUnion([Q0]), "operationType" : NewBodyOperationType.REMOVE, "oppositeDirection" : true, "depth" : 1 * mm, "offsetDistance" : 25 * mm});
        }
        {
            var Q0;
            Q0 = qSketchRegion(id + "F6", true);
            var Q1;
            Q1 = qConstructionFilter(qBodyType(qCreatedBy(id + "F6" ,EDGE), BodyType.WIRE), ConstructionObject.NO);
            extrude(context, id + "F8", {"entities" : qUnion([Q0]), "operationType" : NewBodyOperationType.REMOVE, "surfaceEntities" : qUnion([Q1]), "oppositeDirection" : true, "depth" : 25.4 * mm / 8 + 1 * mm, "offsetDistance" : 25 * mm});
        }
    });
